# Revit family: Naughtone_Tbls_Fold_850SquareCafe
name_source: partatom
category: Furniture
revit_build: Autodesk Revit 2015 (Build: 20160512_1515(x64)
units: mm (PartAtom-declared; Revit-internal decimal feet)

## types (1)
- Naughtone_Tbls_Fold_850SquareCafe
    AdditionalMaterials = Additional material and finish options available. Please contact Naughtone direct for further information.
    Assembly Code = E2020200
    AssetType = Movable
    BIMObjectName = Naughtone_Tables_Fold_850SquareCafe
    Category = Pr_40_50_21: Desks, tables and worktops
    Cost = 0 $
    Description = Fold 850 Square Cafe Table
    DurationUnit = year
    IfcExportAs = IfcFurnishingElementType
    IfcExportType = TABLE
    Keynote = Pr_40_50_21
    ManufacturerAddressUK = Knaresborough Tech Park, Manse Lane, Knaresborough, HG5 8LF
    ManufacturerName = Naughtone
    ManufacturerURL = www.naughtone.com/
    Material = Mild Steel
    Model = FOLD-850-SQ
    ModelNumber = FOLD-850-SQ
    ModelReference = Fold 850 Square Cafe Table
    NBSDescription = Tables
    NBSReference = 45-35-86/327
    Name = Tables_Fold_850SquareCafe_Naughtone
    NominalHeight = 750 mm  [stored 2.46063 ft]
    NominalLength = 850 mm  [stored 2.78871 ft]
    NominalWidth = 850 mm  [stored 2.78871 ft]
    NumberOfChairs = 0
    ProductInformation = www.naughtone.com/portfolio-view/fold
    Shape = Square
    Size = 850mmx850mmx750mm
    URL = http://www.naughtone.com
    Uniclass2015Description = Desks, tables and worktops
    Uniclass2015Reference = Pr_40_50_21
    Uniclass2015Version = Products v1.3
    Version = 1
    WarrantyDescription = Request warranty information from naughtone
    WarrantyDurationLabor = 5
    WarrantyDurationParts = 5
    WarrantyDurationUnit = year
    WorksurfaceArea = 0 m²

note: [stored X ft] marks values corroborated as IEEE doubles in the binary element streams (Revit-internal decimal feet)

## geometry (parser evidence)
native form markers: Sweep x5
no freeform markers — native parametric forms only
